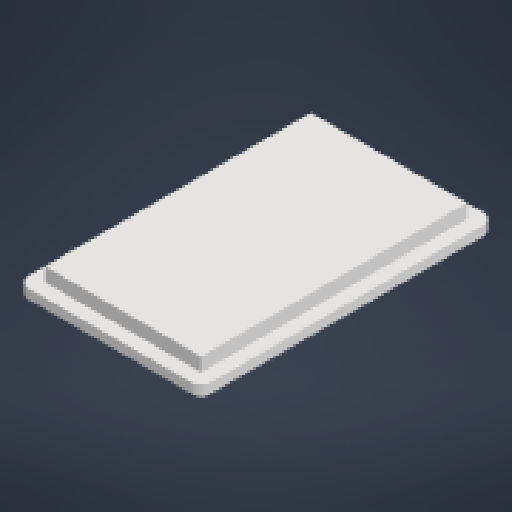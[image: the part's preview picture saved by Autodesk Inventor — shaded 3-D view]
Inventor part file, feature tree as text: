
AUTODESK INVENTOR PART (.ipt)
format: ipt  version: 2024 (Build 280153000, 153)  size: 199,168 bytes
history: native  units: mm
features: reference x16, other x4, extrude x3, sketch x3, fillet x1, shell x1
ambient origin geometry x8: Origin, YZ Plane, XZ Plane, XY Plane, X Axis, Y Axis, Z Axis, Center Point
bodies: Body1 (feature_tree)
feature tree (28):
  other  "Твердое тело1"
  extrude  "Выдавливание1"  Depth=2.0mm
  extrude  "Выдавливание2"  Depth=5.0mm TaperAngle=0.0deg
  extrude  "Выдавливание3"  Depth=3.5mm TaperAngle=0.0deg
  fillet  "Сопряжение2"  Radius=3.0mm
  shell  "Оболочка1"  Thickness=3.0mm
  sketch  "Эскиз1"
  reference  "Ссылка1"
  reference  "Ссылка2"
  reference  "Ссылка3"
  reference  "Ссылка4"
  reference  "Ссылка5"
  reference  "Ссылка6"
  reference  "Ссылка7"
  reference  "Ссылка8"
  sketch  "Эскиз2"
  reference  "Ссылка9"
  reference  "Ссылка10"
  reference  "Ссылка11"
  reference  "Ссылка12"
  reference  "Ссылка13"
  reference  "Ссылка14"
  reference  "Ссылка15"
  reference  "Ссылка16"
  sketch  "Эскиз3"
  parser-record x1  (decoder bookkeeping rows leaked as tree rows — omitted from the tree; the rows remain in map.json)
  other  "back_box_asembly.iam"
  other  "back_box_mid:1"
note: 1 file-system path scrubbed to <path> (originals preserved in map.json)
